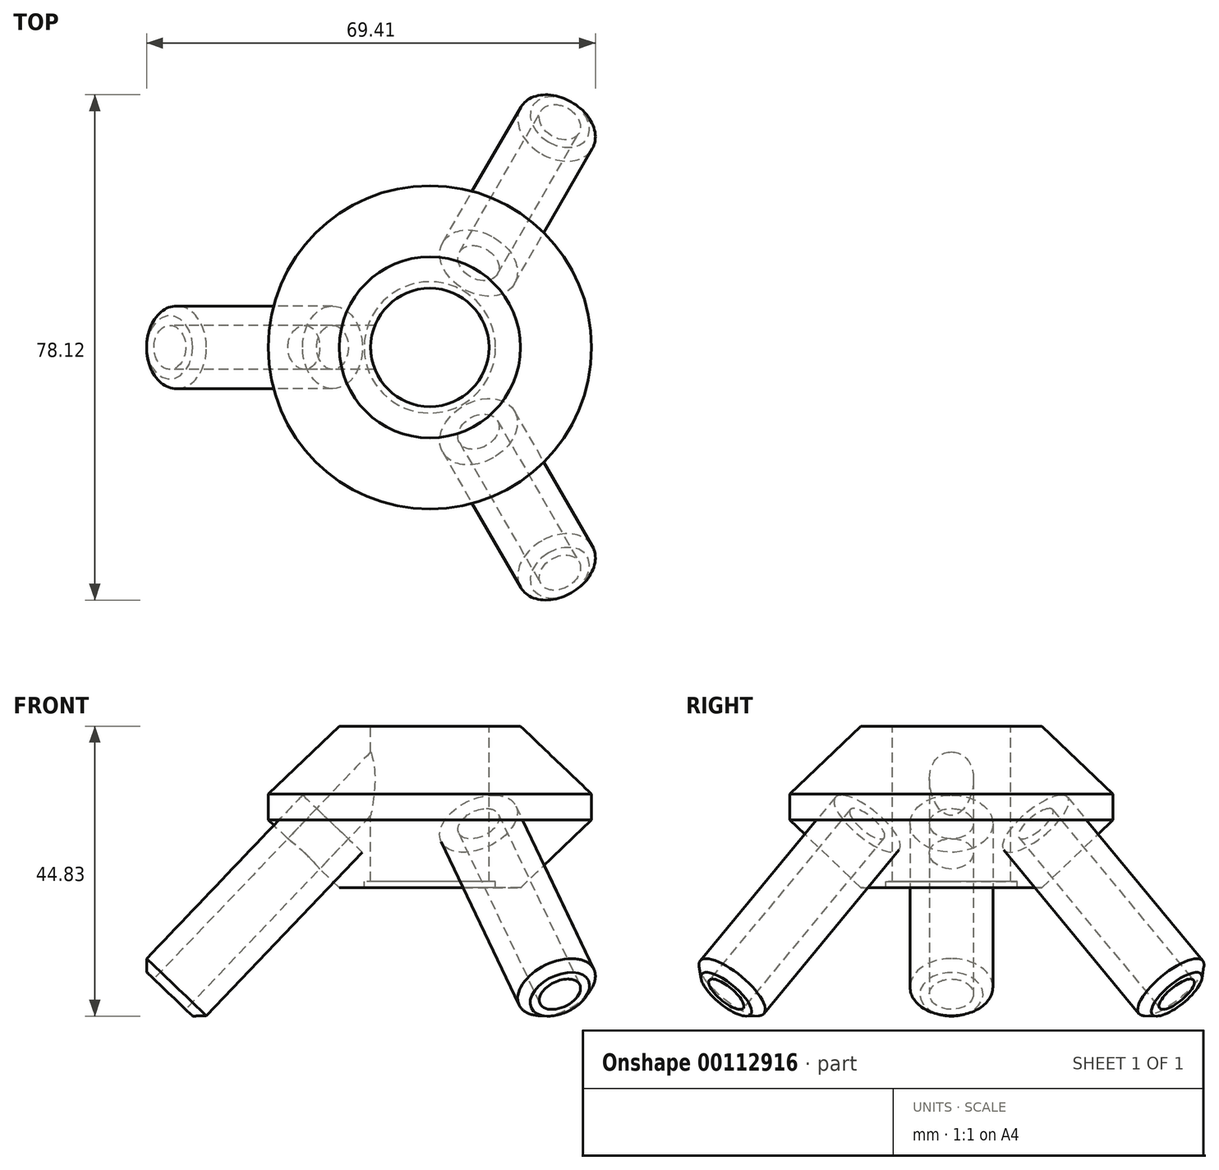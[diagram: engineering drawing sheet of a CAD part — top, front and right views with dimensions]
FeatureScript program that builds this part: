
annotation { "Feature Type Name" : "Feature", "Feature Type Description" : "" }
export const myFeature = defineFeature(function(context is Context, id is Id, definition is map)
    precondition{}
    {
        {
            var Q0;
            Q0=qCreatedBy(makeId("Front.planeOp"),FACE);
            var sketch = newSketch(context, id + "F0", { "sketchPlane" : qUnion([Q0])});
            skLineSegment(sketch, "E0", {"start": v(-9.15, 25) * mm, "end": v(-14, 25) * mm});
            skLineSegment(sketch, "E1", {"start": v(-14, 25) * mm, "end": v(-25, 14.5) * mm});
            skLineSegment(sketch, "E2", {"start": v(-25, 14.5) * mm, "end": v(-25, 10.5) * mm});
            skLineSegment(sketch, "E3", {"start": v(-25, 10.5) * mm, "end": v(-14, 0) * mm});
            skPoint(sketch, "E4.end.orphan", {"position": v(0, 65) * mm});
            skLineSegment(sketch, "E5", {"start": v(-9.15, 25) * mm, "end": v(-9.15, 1) * mm});
            skPoint(sketch, "E6.orphan", {"position": v(0, 25) * mm});
            skLineSegment(sketch, "E7", {"start": v(-14, 0) * mm, "end": v(-10.15, 0) * mm});
            skLineSegment(sketch, "E8", {"start": v(-10.15, 0) * mm, "end": v(-10.15, 1) * mm});
            skLineSegment(sketch, "E9", {"start": v(-10.15, 1) * mm, "end": v(-9.15, 1) * mm});
            skLineSegment(sketch, "E10", {"start": v(0, 25) * mm, "end": v(0, 0) * mm, "construction": true});
            skSolve(sketch);
        }
        {
            var Q0;
            Q0=makeQuery(id+"F0.imprint","IMPRINT",FACE,{"disambiguationData":[TD([[makeQuery(id+"F0.imprint","IMPRINT",EDGE,{"derivedFrom":sQuery(id+"F0.wireOp",EDGE,"E0")}),1.0]])]});
            var Q1;
            Q1=sQuery(id+"F0.wireOp",EDGE,"E10");
            revolve(context, id + "F1", {"entities" : qUnion([Q0]), "axis" : qUnion([Q1]), "revolveType" : RevolveType.FULL});
        }
        {
            var Q0;
            Q0=qCreatedBy(makeId("Front.planeOp"),FACE);
            var sketch = newSketch(context, id + "F2", { "sketchPlane" : qUnion([Q0])});
            skLineSegment(sketch, "E11", {"start": v(-14.87, 0.83) * mm, "end": v(-35.58, -20.87) * mm});
            skLineSegment(sketch, "E12", {"start": v(-35.58, -20.87) * mm, "end": v(-40.21, -16.45) * mm});
            skLineSegment(sketch, "E13", {"start": v(-40.21, -16.45) * mm, "end": v(-19.5, 5.25) * mm});
            skLineSegment(sketch, "E14", {"start": v(-19.5, 5.25) * mm, "end": v(-15.05, 9.91) * mm});
            skLineSegment(sketch, "E15", {"start": v(-15.05, 9.91) * mm, "end": v(-10.42, 5.5) * mm});
            skLineSegment(sketch, "E16", {"start": v(-10.42, 5.5) * mm, "end": v(-14.87, 0.83) * mm});
            skSolve(sketch);
        }
        {
            var Q0;
            Q0 = qSketchRegion(id + "F2", true);
            var Q1;
            Q1=sQuery(id+"F2.wireOp",EDGE,"E13");
            revolve(context, id + "F3", {"entities" : qUnion([Q0]), "axis" : qUnion([Q1]), "revolveType" : RevolveType.FULL});
        }
        {
            var Q0;
            Q0=makeQuery(id+"F3.opRevolve","SWEPT_FACE",FACE,{"disambiguationData":[OSD([sQuery(id+"F2.wireOp",EDGE,"E12")])]});
            var sketch = newSketch(context, id + "F4", { "sketchPlane" : qUnion([Q0])});
            skCircle(sketch, "E17", {"center": v(-17.73, 0) * mm, "radius": 3.4 * mm});
            skSolve(sketch);
        }
        {
            var Q0;
            Q0 = qSketchRegion(id + "F4", true);
            extrude(context, id + "F5", {"entities" : qUnion([Q0]), "operationType" : NewBodyOperationType.REMOVE, "endBound" : BoundingType.THROUGH_ALL, "oppositeDirection" : true, "depth" : 25 * mm});
        }
        {
            var Q0;
            Q0=makeQuery(id+"F3.opRevolve","SWEPT_EDGE",EDGE,{"disambiguationData":[OSD([sQuery(id+"F2.wireOp",EDGE,"E11"),sQuery(id+"F2.wireOp",EDGE,"E12")])]});
            chamfer(context, id + "F6", {"entities" : qUnion([Q0]), "width" : 1.5 * mm, "tangentPropagation" : true});
        }
        {
            var Q0;
            Q0=makeQuery(id+"F3.opRevolve","SWEPT_BODY",BODY,{"disambiguationData":[OSD([sQuery(id+"F2.wireOp",EDGE,"E11"),sQuery(id+"F2.wireOp",EDGE,"E12"),sQuery(id+"F2.wireOp",EDGE,"E13"),sQuery(id+"F2.wireOp",EDGE,"E14"),sQuery(id+"F2.wireOp",EDGE,"E15"),sQuery(id+"F2.wireOp",EDGE,"E16")])]});
            var Q1;
            Q1=makeQuery(id+"F1.opRevolve","SWEPT_FACE",FACE,{"disambiguationData":[OSD([sQuery(id+"F0.wireOp",EDGE,"E2")])]});
            circularPattern(context, id + "F7", {"entities" : qUnion([Q0]), "axis" : qUnion([Q1]), "angle" : 360 * degree, "instanceCount" : 3, "equalSpace" : true});
        }
    });
